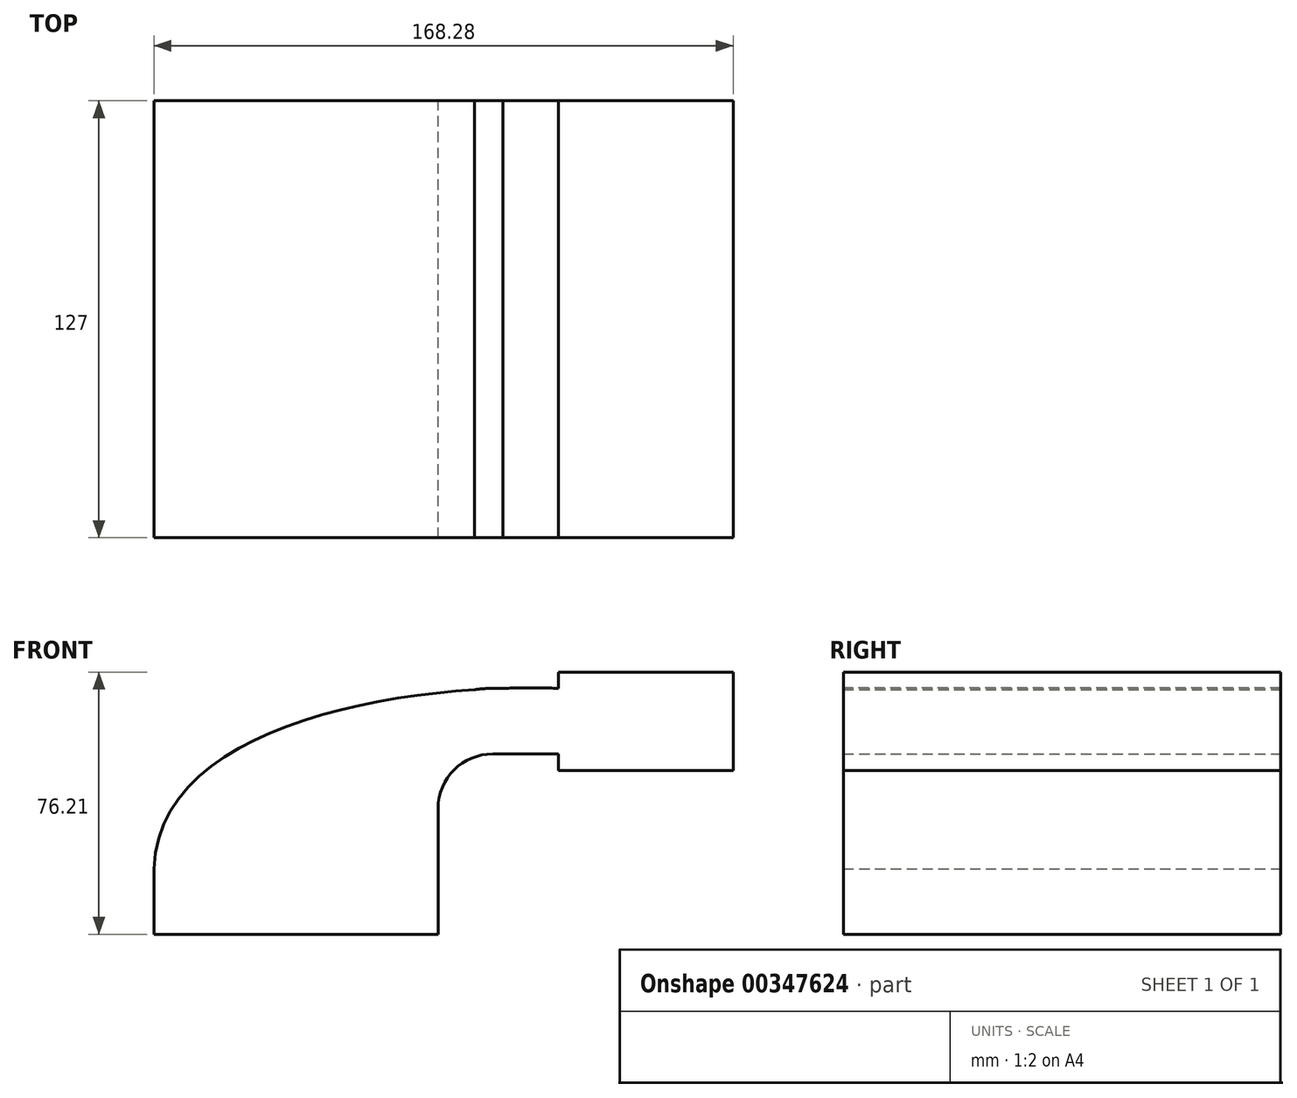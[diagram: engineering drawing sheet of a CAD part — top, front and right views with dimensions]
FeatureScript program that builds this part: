
annotation { "Feature Type Name" : "Feature", "Feature Type Description" : "" }
export const myFeature = defineFeature(function(context is Context, id is Id, definition is map)
    precondition{}
    {
        {
            var Q0;
            Q0=qCreatedBy(makeId("Front.planeOp"),FACE);
            var sketch = newSketch(context, id + "F0", { "sketchPlane" : qUnion([Q0])});
            skLineSegment(sketch, "E0.bottom", {"start": v(41.28, -9.53) * mm, "end": v(-41.28, -9.53) * mm});
            skLineSegment(sketch, "E0.top", {"start": v(41.27, 9.53) * mm, "end": v(-41.27, 9.52) * mm});
            skLineSegment(sketch, "E0.left", {"start": v(41.28, -9.53) * mm, "end": v(41.27, 9.53) * mm});
            skLineSegment(sketch, "E0.right", {"start": v(-41.27, -9.53) * mm, "end": v(-41.28, 9.52) * mm});
            skPoint(sketch, "E0.middle", {"position": v(0, 0) * mm});
            skLineSegment(sketch, "E1.bottom", {"start": v(127, 38.1) * mm, "end": v(76.2, 38.1) * mm});
            skLineSegment(sketch, "E1.top", {"start": v(127, 66.68) * mm, "end": v(76.2, 66.68) * mm});
            skLineSegment(sketch, "E1.left", {"start": v(127, 38.1) * mm, "end": v(127, 66.68) * mm});
            skLineSegment(sketch, "E1.right", {"start": v(76.2, 38.1) * mm, "end": v(76.2, 66.68) * mm});
            skPoint(sketch, "E1.middle", {"position": v(101.6, 52.39) * mm});
            skLineSegment(sketch, "E2", {"start": v(41.27, 0) * mm, "end": v(41.27, 27) * mm});
            skArc(sketch, "E3", {"start": v(41.27, 27) * mm, "mid": v(45.92, 38.23) * mm, "end": v(57.15, 42.88) * mm});
            skLineSegment(sketch, "E4", {"start": v(57.15, 42.88) * mm, "end": v(101.6, 42.88) * mm});
            skPoint(sketch, "E4.endSnap0", {"position": v(101.6, 38.1) * mm});
            skLineSegment(sketch, "E5.0", {"start": v(57.15, 61.93) * mm, "end": v(101.6, 61.93) * mm});
            skArc(sketch, "E5.1", {"start": v(22.22, 27) * mm, "mid": v(32.45, 51.7) * mm, "end": v(57.15, 61.93) * mm});
            skLineSegment(sketch, "E5.2", {"start": v(22.22, 9.53) * mm, "end": v(22.22, 27) * mm});
            skLineSegment(sketch, "E6", {"start": v(101.6, 66.68) * mm, "end": v(101.6, 38.1) * mm});
            skFitSpline(sketch, "E7", {"points": [v(-41.28, 9.52) * mm, v(76.2, 61.93) * mm], "startDerivative": vector(4.21, 129.95) * mm, "endDerivative": vector(128.34, -4.52) * mm});
            skSolve(sketch);
        }
        {
            var Q0;
            Q0 = qSketchRegion(id + "F0", true);
            extrude(context, id + "F1", {"entities" : qUnion([Q0]), "depth" : 127 * mm, "symmetric" : true});
        }
    });
